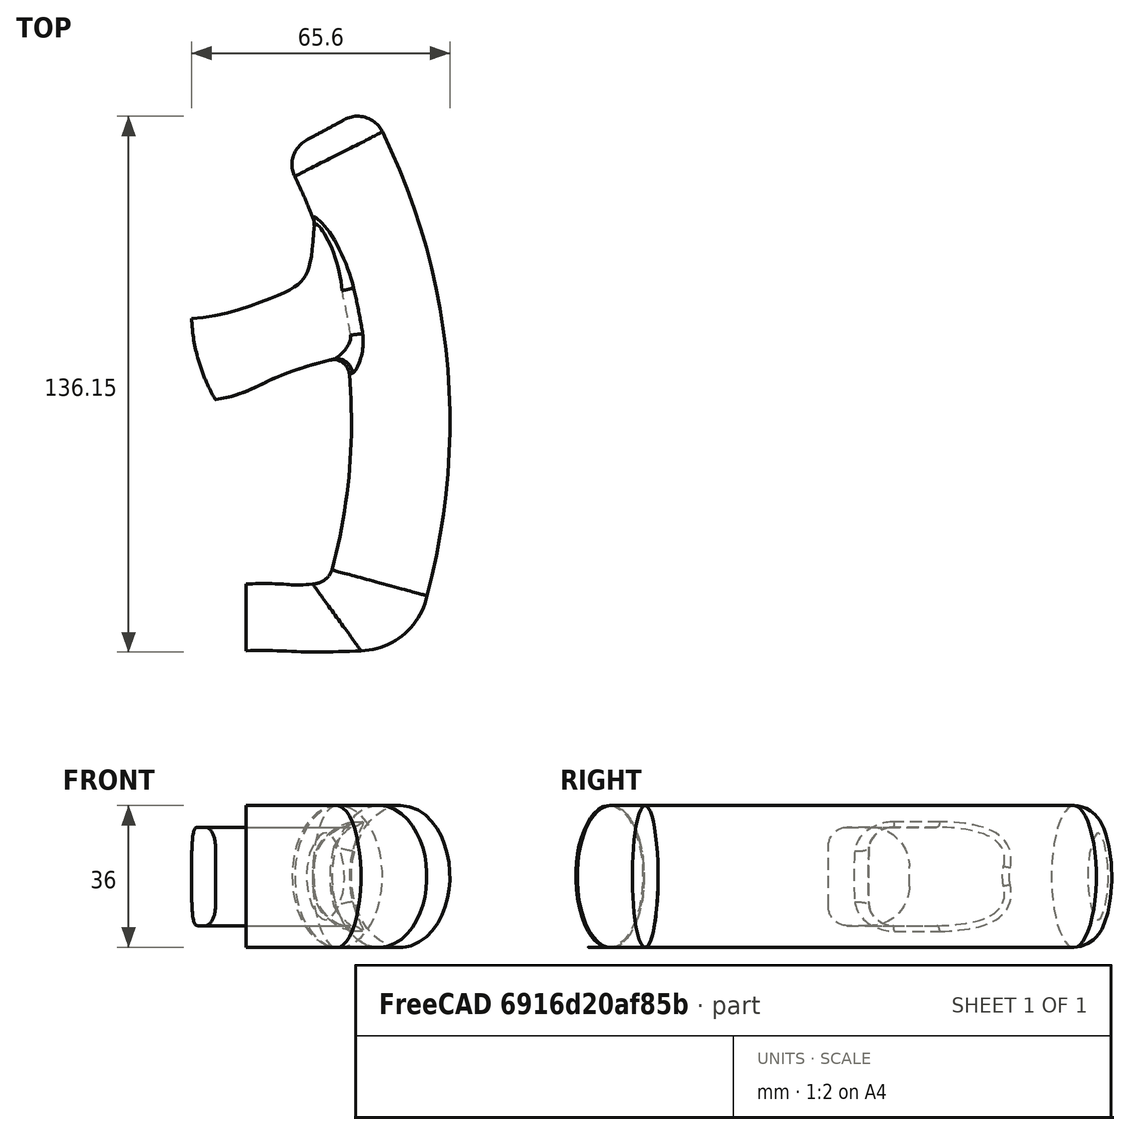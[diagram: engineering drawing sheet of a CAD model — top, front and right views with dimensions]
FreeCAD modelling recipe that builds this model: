
FCSTD DOCUMENT  (FreeCAD 1.0R39109 (Git))
Label: handle-5mk2
License: All rights reserved
LicenseURL: https://en.wikipedia.org/wiki/All_rights_reserved
objects: Sketcher::SketchObject×24, PartDesign::Plane×14, PartDesign::Fillet×6, PartDesign::AdditivePipe×3, Mesh::Feature×1, PartDesign::Pad×1, PartDesign::Body×1
note: 93 computed .brp shape members not serialized (recipe doc carries the construction recipe); baked Part::Feature solids carry a one-line shape summary decoded from their .brp

FEATURE [Sketcher::SketchObject] Sketch  label="draft"
  ArcFitTolerance = 1e-06
  FullyConstrained = false
  MakeInternals = false
  sketch-geometry (31):
    g0: LineSegment StartX=0 StartY=16.8405 StartZ=0 EndX=0 EndY=0 EndZ=0
    g1: ArcOfCircle CenterX=24.2442 CenterY=17 CenterZ=0 NormalX=0 NormalY=0 NormalZ=1 AngleXU=0 Radius=17 StartAngle=4.71239 EndAngle=6.01234
    g2: ArcOfCircle CenterX=12.089 CenterY=21.8405 CenterZ=0 NormalX=0 NormalY=0 NormalZ=1 AngleXU=0 Radius=5 StartAngle=4.71239 EndAngle=6.02249
    g3: ArcOfCircle CenterX=0 CenterY=8.42024 CenterZ=0 NormalX=0 NormalY=0 NormalZ=1 AngleXU=0 Radius=8.42024 StartAngle=1.5708 EndAngle=4.71239
    g4: LineSegment StartX=12.089 StartY=16.8405 StartZ=0 EndX=12.089 EndY=0 EndZ=0
    g5: LineSegment StartX=15.135 StartY=17.8754 StartZ=0 EndX=34.532 EndY=3.46632 EndZ=0
    g6: LineSegment StartX=12.089 StartY=16.8405 StartZ=0 EndX=24.2442 EndY=-0.00123973 EndZ=0
    g7: LineSegment StartX=16.92 StartY=20.5517 StartZ=0 EndX=40.6245 EndY=12.4517 EndZ=0
    g8: LineSegment StartX=12.089 StartY=16.8405 StartZ=0 EndX=17.9725 EndY=-3.6e-15 EndZ=0
    g9: LineSegment StartX=8.25203 StartY=67.8671 StartZ=0 EndX=4.47332 EndY=84.6059 EndZ=0
    g10: ArcOfCircle CenterX=6.36268 CenterY=76.2365 CenterZ=0 NormalX=0 NormalY=0 NormalZ=1 AngleXU=0 Radius=8.58001 StartAngle=1.79282 EndAngle=4.93441
    g11: LineSegment StartX=4.3823 StartY=126.388 StartZ=0 EndX=26.3634 EndY=138.297 EndZ=0
    g12: LineSegment StartX=0 StartY=0 StartZ=0 EndX=24.2442 EndY=0 EndZ=0
    g13: LineSegment StartX=12.089 StartY=16.8405 StartZ=0 EndX=0 EndY=16.8405 EndZ=0
    g14: ArcOfCircle CenterX=-122.373 CenterY=57.711 CenterZ=0 NormalX=0 NormalY=0 NormalZ=1 AngleXU=0 Radius=169.165 StartAngle=6.01234 EndAngle=6.77971
    g15: LineSegment StartX=34.0166 StartY=141.401 StartZ=0 EndX=34.0166 EndY=126.047 EndZ=0
    g16: LineSegment StartX=34.0166 StartY=141.401 StartZ=0 EndX=31.941 EndY=152.351 EndZ=0
    g17: LineSegment StartX=22.7796 StartY=155.606 StartZ=0 EndX=28.011 EndY=155.606 EndZ=0
    g18: LineSegment StartX=18.3769 StartY=88.901 StartZ=0 EndX=4.47332 EndY=84.6059 EndZ=0
    g19: LineSegment StartX=21.1969 StartY=70.7893 StartZ=0 EndX=8.25203 EndY=67.8671 EndZ=0
    g20: LineSegment StartX=18.7796 StartY=146.991 StartZ=0 EndX=18.7796 EndY=151.606 EndZ=0
    g21: LineSegment StartX=15.6305 StartY=135.869 StartZ=0 EndX=18.5135 EndY=145.224 EndZ=0
    g22: ArcOfCircle CenterX=12.7796 CenterY=146.991 CenterZ=0 NormalX=0 NormalY=0 NormalZ=1 AngleXU=0 Radius=6 StartAngle=5.98426 EndAngle=6.28319
    g23: ArcOfCircle CenterX=5.11835 CenterY=139.108 CenterZ=0 NormalX=0 NormalY=0 NormalZ=1 AngleXU=0 Radius=11 StartAngle=5.12409 EndAngle=5.98426
    g24: ArcOfCircle CenterX=27.9086 CenterY=86.9159 CenterZ=0 NormalX=0 NormalY=0 NormalZ=1 AngleXU=0 Radius=45.9511 StartAngle=1.9825 EndAngle=2.10829
    g25: ArcOfCircle CenterX=22.7796 CenterY=151.606 CenterZ=0 NormalX=0 NormalY=0 NormalZ=1 AngleXU=0 Radius=4 StartAngle=1.5708 EndAngle=3.14159
    g26: ArcOfCircle CenterX=28.011 CenterY=151.606 CenterZ=0 NormalX=0 NormalY=0 NormalZ=1 AngleXU=0 Radius=4 StartAngle=0.187333 EndAngle=1.5708
    g27: ArcOfCircle CenterX=54.0166 CenterY=126.047 CenterZ=0 NormalX=0 NormalY=0 NormalZ=1 AngleXU=0 Radius=20 StartAngle=3.14159 EndAngle=3.5112
    g28: ArcOfCircle CenterX=-122.373 CenterY=57.711 CenterZ=0 NormalX=0 NormalY=0 NormalZ=1 AngleXU=0 Radius=144.165 StartAngle=6.02249 EndAngle=6.37403
    g29: ArcOfCircle CenterX=-122.373 CenterY=57.711 CenterZ=0 NormalX=0 NormalY=0 NormalZ=1 AngleXU=0 Radius=144.165 StartAngle=0.218074 EndAngle=0.496528
    g30: ArcOfCircle CenterX=-122.373 CenterY=57.711 CenterZ=0 NormalX=0 NormalY=0 NormalZ=1 AngleXU=0 Radius=156.665 StartAngle=6.01234 EndAngle=6.77971
  constraints (1):
    c: Distance(g6,g6) = 20.77
FEATURE [Sketcher::SketchObject] Sketch001  label="main"
  ArcFitTolerance = 1e-06
  AttachmentSupport = -> [XY_Plane]
  FullyConstrained = false
  MakeInternals = false
  MapMode = 5
  sketch-geometry (33):
    g0: LineSegment StartX=0 StartY=0 StartZ=0 EndX=3e-16 EndY=17 EndZ=0
    g1: LineSegment StartX=3e-16 StartY=17 StartZ=0 EndX=11.9553 EndY=17 EndZ=0
    g2: ArcOfCircle CenterX=0.098169 CenterY=8.5 CenterZ=0 NormalX=0 NormalY=0 NormalZ=1 AngleXU=0 Radius=8.50057 StartAngle=1.58235 EndAngle=4.70084
    g3: LineSegment StartX=4.3731 StartY=126.451 StartZ=0 EndX=26.3546 EndY=138.359 EndZ=0
    g4: ArcOfCircle CenterX=-121.158 CenterY=57.9598 CenterZ=0 NormalX=0 NormalY=0 NormalZ=1 AngleXU=0 Radius=168 StartAngle=6.01838 EndAngle=6.78221
    g5: ArcOfCircle CenterX=-121.158 CenterY=57.9598 CenterZ=0 NormalX=0 NormalY=0 NormalZ=1 AngleXU=0 Radius=143 StartAngle=6.01836 EndAngle=6.78265
    g6: ArcOfCircle CenterX=11.9915 CenterY=22.1177 CenterZ=0 NormalX=0 NormalY=0 NormalZ=1 AngleXU=0 Radius=5.11783 StartAngle=4.70532 EndAngle=5.96793
    g7: LineSegment StartX=40.9861 StartY=13.99 StartZ=0 EndX=16.8571 EndY=20.5309 EndZ=0
    g8: ArcOfCircle CenterX=23.8596 CenterY=17.4727 CenterZ=0 NormalX=0 NormalY=0 NormalZ=1 AngleXU=0 Radius=17.4771 StartAngle=4.73473 EndAngle=6.08257
    g9: LineSegment StartX=33.9499 StartY=141.42 StartZ=0 EndX=32 EndY=152 EndZ=0
    g10: LineSegment StartX=19 StartY=152 StartZ=0 EndX=18.6911 EndY=146 EndZ=0
    g11: LineSegment StartX=22 StartY=155.6 StartZ=0 EndX=29 EndY=155.6 EndZ=0
    g12: ArcOfCircle CenterX=28.2135 CenterY=151.895 CenterZ=0 NormalX=0 NormalY=0 NormalZ=1 AngleXU=0 Radius=3.78792 StartAngle=0.027823 EndAngle=1.36165
    g13: ArcOfCircle CenterX=22.5443 CenterY=152.096 CenterZ=0 NormalX=0 NormalY=0 NormalZ=1 AngleXU=0 Radius=3.5456 StartAngle=1.72492 EndAngle=3.16879
    g14: LineSegment StartX=4.41682 StartY=84.6096 StartZ=0 EndX=8.23235 EndY=68.0434 EndZ=0
    g15: ArcOfCircle CenterX=6.32458 CenterY=76.3265 CenterZ=0 NormalX=0 NormalY=0 NormalZ=1 AngleXU=0 Radius=8.5 StartAngle=1.79717 EndAngle=4.93946
    g16: LineSegment StartX=4.42825 StartY=84.5878 StartZ=0 EndX=18.4319 EndY=88.947 EndZ=0
    g17: LineSegment StartX=8.23235 StartY=68.0434 StartZ=0 EndX=21.1452 EndY=72.063 EndZ=0
    g18: LineSegment StartX=32.5262 StartY=20 StartZ=0 EndX=28.9216 EndY=17.2604 EndZ=0
    g19: LineSegment StartX=11.9553 StartY=17 StartZ=0 EndX=24.25 EndY=5.33e-14 EndZ=0
    g20: LineSegment StartX=14.9929 StartY=17.9724 StartZ=0 EndX=35.0562 EndY=4.05322 EndZ=0
    g21: LineSegment StartX=16.2172 StartY=19.2306 StartZ=0 EndX=39.0494 EndY=8.82884 EndZ=0
    g22: LineSegment StartX=13.6942 StartY=17.2914 StartZ=0 EndX=30.2927 EndY=1.22269 EndZ=0
    g23: LineSegment StartX=10.6374 StartY=17 StartZ=0 EndX=17.3604 EndY=0 EndZ=0
    g24: LineSegment StartX=9.44468 StartY=17 StartZ=0 EndX=12.125 EndY=0 EndZ=0
    g25: LineSegment StartX=8.01497 StartY=17 StartZ=0 EndX=8.01497 EndY=0 EndZ=0
    g26: LineSegment StartX=5.97763 StartY=17 StartZ=0 EndX=5.97763 EndY=0 EndZ=0
    g27: LineSegment StartX=20.8595 StartY=74.6968 StartZ=0 EndX=45.6917 EndY=77.5875 EndZ=0
    g28: LineSegment StartX=0 StartY=0 StartZ=0 EndX=8.01497 EndY=0 EndZ=0
    g29: LineSegment StartX=8.01497 StartY=0 StartZ=0 EndX=24.25 EndY=0 EndZ=0
    g30: LineSegment StartX=15.3638 StartY=132.405 StartZ=0 EndX=18.6911 EndY=146 EndZ=0
    g31: LineSegment StartX=33.9499 StartY=141.42 StartZ=0 EndX=35.5663 EndY=109.757 EndZ=0
    g32: LineSegment StartX=15.3638 StartY=132.405 StartZ=0 EndX=35.5663 EndY=109.757 EndZ=0
  constraints (60):
    c: PointOnObject(g8,g-1)
    c: Distance(g0) = 17
    c: PointOnObject(g0,g-2)
    c: DistanceX(g-1,g8) = 24.25
    c: Coincident(g1,g0)
    c: Horizontal(g1)
    c: Coincident(g2,g0)
    c: Distance(g3) = 25
    c: Coincident(g4,g3)
    c: Radius(g4) = 168
    c: Coincident(g5,g4)
    c: Coincident(g5,g3)
    c: Coincident(g6,g1)
    c: Coincident(g6,g5)
    c: Coincident(g7,g4)
    c: Coincident(g7,g5)
    c: DistanceY(g-1,g4) = 13.99
    c: Coincident(g8,g4)
    c: Horizontal(g11)
    c: Coincident(g12,g11)
    c: Coincident(g12,g9)
    c: Coincident(g13,g11)
    c: Coincident(g13,g10)
    c: Distance(g14) = 17
    c: Symmetric(g14,g14,g15)
    c: Coincident(g15,g14)
    c: Coincident(g17,g14)
    c: PointOnObject(g17,g5)
    c: Parallel(g17,g16)
    c: Symmetric(g7,g7,g18)
    c: Coincident(g19,g1)
    c: PointOnObject(g20,g6)
    c: PointOnObject(g20,g8)
    c: PointOnObject(g21,g6)
    c: PointOnObject(g21,g8)
    c: PointOnObject(g22,g6)
    c: PointOnObject(g22,g8)
    c: PointOnObject(g23,g1)
    c: PointOnObject(g24,g1)
    c: Symmetric(g-1,g8,g24)
    c: PointOnObject(g25,g1)
    c: Vertical(g25)
    c: Symmetric(g1,g1,g26)
    c: Vertical(g26)
    c: PointOnObject(g27,g5)
    c: PointOnObject(g27,g4)
    c: Distance(g19,g19) = 20.98
    c: Distance(g21,g21) = 25.09
    c: Distance(g24,g24) = 17.21
    c: Coincident(g28,g0)
    c: Coincident(g28,g25)
    c: Horizontal(g28)
    c: Coincident(g29,g25)
    c: Coincident(g29,g8)
    c: Horizontal(g29)
    c: Symmetric(g3,g3,g30)
    c: Coincident(g30,g10)
    c: Coincident(g31,g9)
    c: Coincident(g32,g30)
    c: Coincident(g32,g31)
FEATURE [PartDesign::Plane] DatumPlane001
  AttachmentOffset = pos=(0,0,0) rot=(0,1,0;1.5708rad)
  AttachmentSupport = -> [Sketch001]
  Length = 197.115
  MapMode = 7
  Placement = pos=(40.9861,13.99,0) rot=(0.093727,0.703994,0.703994;2.95468rad)
  ResizeMode = 0
  Width = 68.8804
FEATURE [PartDesign::Plane] DatumPlane002
  AttachmentOffset = pos=(0,0,0) rot=(0,1,0;1.5708rad)
  AttachmentSupport = -> [Sketch001]
  Length = 181.364
  MapMode = 7
  Placement = pos=(0,0,0) rot=(0.57735,0.57735,0.57735;2.0944rad)
  ResizeMode = 0
  Width = 68.0717
FEATURE [PartDesign::Plane] DatumPlane
  AttachmentOffset = pos=(0,0,0) rot=(0,1,0;1.5708rad)
  AttachmentSupport = -> [Sketch001]
  Length = 221.295
  MapMode = 7
  Placement = pos=(4.3731,126.451,0) rot=(0.941347,0.238607,0.238607;1.6312rad)
  ResizeMode = 0
  Width = 70.0616
FEATURE [Sketcher::SketchObject] Sketch002
  ArcFitTolerance = 1e-06
  AttachmentSupport = -> [DatumPlane]
  FullyConstrained = false
  MakeInternals = false
  MapMode = 5
  Placement = pos=(4.3731,126.451,0) rot=(0.941347,0.238607,0.238607;1.6312rad)
  sketch-geometry (5):
    g0: Ellipse CenterX=12.5 CenterY=0 CenterZ=0 NormalX=0 NormalY=0 NormalZ=1 MajorRadius=18 MinorRadius=12.5 AngleXU=1.5708
    g1: LineSegment [constr] StartX=12.5 StartY=18 StartZ=0 EndX=12.5 EndY=-18 EndZ=0
    g2: LineSegment [constr] StartX=0 StartY=0 StartZ=0 EndX=25 EndY=0 EndZ=0
    g3: GeomPoint [constr] X=12.5 Y=12.9518 Z=0
    g4: GeomPoint [constr] X=12.5 Y=-12.9518 Z=0
  constraints (2):
    c: InternalAlignment(g1-g4 -> g0) x4
    c: PointOnObject(g-1,g0)
FEATURE [Sketcher::SketchObject] Sketch004
  ArcFitTolerance = 1e-06
  AttachmentOffset = pos=(0,0,-5) rot=(0,0,1;0rad)
  AttachmentSupport = -> [DatumPlane002]
  FullyConstrained = false
  MakeInternals = false
  MapMode = 5
  Placement = pos=(-5,0,0) rot=(0.57735,0.57735,0.57735;2.0944rad)
  sketch-geometry (5):
    g0: Ellipse CenterX=8.5 CenterY=0 CenterZ=0 NormalX=0 NormalY=0 NormalZ=1 MajorRadius=18 MinorRadius=8.5 AngleXU=1.5708
    g1: LineSegment [constr] StartX=8.5 StartY=18 StartZ=0 EndX=8.5 EndY=-18 EndZ=0
    g2: LineSegment [constr] StartX=0 StartY=0 StartZ=0 EndX=17 EndY=0 EndZ=0
    g3: GeomPoint [constr] X=8.5 Y=15.8666 Z=0
    g4: GeomPoint [constr] X=8.5 Y=-15.8666 Z=0
  constraints (2):
    c: InternalAlignment(g1-g4 -> g0) x4
    c: PointOnObject(g-1,g0)
FEATURE [PartDesign::AdditivePipe] AdditivePipe
  AuxilleryCurvelinear = true
  AuxillerySpineTangent = false
  Binormal = (0,0,0)
  Mode = 0
  Placement = pos=(4.3731,126.451,0) rot=(0.941347,0.238607,0.238607;1.6312rad)
  Profile = -> Sketch002
  Refine = true
  Spine = -> Sketch001 [Edge8]
  SpineTangent = false
  Suppressed = false
  Transformation = 0
  Transition = 0
FEATURE [PartDesign::Plane] DatumPlane004
  AttachmentOffset = pos=(0,0,0) rot=(0,1,0;1.5708rad)
  AttachmentSupport = -> [Sketch001]
  Length = 228.856
  MapMode = 7
  Placement = pos=(14.9929,17.9724,0) rot=(-0.91446,0.28615,0.28615;4.62309rad)
  ResizeMode = 0
  Width = 70.4176
FEATURE [Sketcher::SketchObject] Sketch006
  ArcFitTolerance = 1e-06
  AttachmentSupport = -> [DatumPlane004]
  FullyConstrained = false
  MakeInternals = false
  MapMode = 5
  Placement = pos=(14.9929,17.9724,0) rot=(0.91446,-0.28615,-0.28615;1.6601rad)
  sketch-geometry (5):
    g0: Ellipse CenterX=12.205 CenterY=0 CenterZ=0 NormalX=0 NormalY=0 NormalZ=1 MajorRadius=18 MinorRadius=12.205 AngleXU=1.5708
    g1: LineSegment [constr] StartX=12.205 StartY=18 StartZ=0 EndX=12.205 EndY=-18 EndZ=0
    g2: LineSegment [constr] StartX=0 StartY=0 StartZ=0 EndX=24.41 EndY=0 EndZ=0
    g3: GeomPoint [constr] X=12.205 Y=13.2302 Z=0
    g4: GeomPoint [constr] X=12.205 Y=-13.2302 Z=0
  constraints (2):
    c: InternalAlignment(g1-g4 -> g0) x4
    c: PointOnObject(g-1,g0)
FEATURE [PartDesign::Plane] DatumPlane005
  AttachmentOffset = pos=(0,0,0) rot=(0,1,0;1.5708rad)
  AttachmentSupport = -> [Sketch001]
  Length = 235.311
  MapMode = 7
  Placement = pos=(11.9553,17,0) rot=(-0.810565,0.414116,0.414116;4.50389rad)
  ResizeMode = 0
  Width = 70.7169
FEATURE [Sketcher::SketchObject] Sketch007
  ArcFitTolerance = 1e-06
  AttachmentSupport = -> [DatumPlane005]
  FullyConstrained = false
  MakeInternals = false
  MapMode = 5
  Placement = pos=(11.9553,17,0) rot=(0.810565,-0.414116,-0.414116;1.77929rad)
  sketch-geometry (5):
    g0: Ellipse CenterX=10.49 CenterY=0 CenterZ=0 NormalX=0 NormalY=0 NormalZ=1 MajorRadius=18 MinorRadius=10.49 AngleXU=1.5708
    g1: LineSegment [constr] StartX=10.49 StartY=18 StartZ=0 EndX=10.49 EndY=-18 EndZ=0
    g2: LineSegment [constr] StartX=0 StartY=0 StartZ=0 EndX=20.98 EndY=0 EndZ=0
    g3: GeomPoint [constr] X=10.49 Y=14.6274 Z=0
    g4: GeomPoint [constr] X=10.49 Y=-14.6274 Z=0
  constraints (2):
    c: InternalAlignment(g1-g4 -> g0) x4
    c: PointOnObject(g-1,g0)
FEATURE [PartDesign::Plane] DatumPlane006
  AttachmentOffset = pos=(0,0,0) rot=(0,1,0;1.5708rad)
  AttachmentSupport = -> [Sketch001]
  Length = 215.238
  MapMode = 7
  Placement = pos=(16.2172,19.2306,0) rot=(-0.955975,0.207499,0.207499;4.66738rad)
  ResizeMode = 0
  Width = 69.772
FEATURE [Sketcher::SketchObject] Sketch008
  ArcFitTolerance = 1e-06
  AttachmentSupport = -> [DatumPlane006]
  FullyConstrained = false
  MakeInternals = false
  MapMode = 5
  Placement = pos=(16.2172,19.2306,0) rot=(0.955975,-0.207499,-0.207499;1.6158rad)
  sketch-geometry (5):
    g0: Ellipse CenterX=12.545 CenterY=0 CenterZ=0 NormalX=0 NormalY=0 NormalZ=1 MajorRadius=18 MinorRadius=12.545 AngleXU=1.5708
    g1: LineSegment [constr] StartX=12.545 StartY=18 StartZ=0 EndX=12.545 EndY=-18 EndZ=0
    g2: LineSegment [constr] StartX=0 StartY=0 StartZ=0 EndX=25.09 EndY=0 EndZ=0
    g3: GeomPoint [constr] X=12.545 Y=12.9083 Z=0
    g4: GeomPoint [constr] X=12.545 Y=-12.9083 Z=0
  constraints (2):
    c: InternalAlignment(g1-g4 -> g0) x4
    c: PointOnObject(g-1,g0)
FEATURE [PartDesign::Plane] DatumPlane007
  AttachmentOffset = pos=(0,0,0) rot=(0,1,0;1.5708rad)
  AttachmentSupport = -> [Sketch001]
  Length = 235.311
  MapMode = 7
  Placement = pos=(11.9553,17,0) rot=(-0.810565,0.414116,0.414116;4.50389rad)
  ResizeMode = 0
  Width = 70.7169
FEATURE [Sketcher::SketchObject] Sketch009  label="Sketch009 7 dupe"
  ArcFitTolerance = 1e-06
  AttachmentSupport = -> [DatumPlane007]
  FullyConstrained = false
  MakeInternals = false
  MapMode = 5
  Placement = pos=(11.9553,17,0) rot=(0.810565,-0.414116,-0.414116;1.77929rad)
  sketch-geometry (5):
    g0: Ellipse CenterX=10.49 CenterY=0 CenterZ=0 NormalX=0 NormalY=0 NormalZ=1 MajorRadius=18 MinorRadius=10.49 AngleXU=1.5708
    g1: LineSegment [constr] StartX=10.49 StartY=18 StartZ=0 EndX=10.49 EndY=-18 EndZ=0
    g2: LineSegment [constr] StartX=0 StartY=0 StartZ=0 EndX=20.98 EndY=0 EndZ=0
    g3: GeomPoint [constr] X=10.49 Y=14.6274 Z=0
    g4: GeomPoint [constr] X=10.49 Y=-14.6274 Z=0
  constraints (2):
    c: InternalAlignment(g1-g4 -> g0) x4
    c: PointOnObject(g-1,g0)
FEATURE [PartDesign::Plane] DatumPlane008
  AttachmentOffset = pos=(0,0,0) rot=(0,1,0;1.5708rad)
  AttachmentSupport = -> [Sketch001]
  Length = 202.306
  MapMode = 7
  Placement = pos=(9.44468,17,0) rot=(-0.63745,0.54482,0.54482;4.2766rad)
  ResizeMode = 0
  Width = 69.1398
FEATURE [Sketcher::SketchObject] Sketch010
  ArcFitTolerance = 1e-06
  AttachmentOffset = pos=(0,0,2) rot=(0,0,1;0rad)
  AttachmentSupport = -> [DatumPlane008]
  FullyConstrained = false
  MakeInternals = false
  MapMode = 5
  Placement = pos=(7.46909,16.6885,2e-16) rot=(0.63745,-0.54482,-0.54482;2.00659rad)
  sketch-geometry (5):
    g0: Ellipse CenterX=8.605 CenterY=0 CenterZ=0 NormalX=0 NormalY=0 NormalZ=1 MajorRadius=18 MinorRadius=8.605 AngleXU=1.5708
    g1: LineSegment [constr] StartX=8.605 StartY=18 StartZ=0 EndX=8.605 EndY=-18 EndZ=0
    g2: LineSegment [constr] StartX=0 StartY=0 StartZ=0 EndX=17.21 EndY=0 EndZ=0
    g3: GeomPoint [constr] X=8.605 Y=15.8099 Z=0
    g4: GeomPoint [constr] X=8.605 Y=-15.8099 Z=0
  constraints (2):
    c: InternalAlignment(g1-g4 -> g0) x4
    c: PointOnObject(g-1,g0)
FEATURE [PartDesign::Plane] DatumPlane009
  AttachmentOffset = pos=(0,0,0) rot=(0,1,0;1.5708rad)
  AttachmentSupport = -> [Sketch001]
  Length = 181.364
  MapMode = 7
  Placement = pos=(8.01497,17,0) rot=(-0.57735,0.57735,0.57735;4.18879rad)
  ResizeMode = 0
  Width = 68.0717
FEATURE [Sketcher::SketchObject] Sketch011
  ArcFitTolerance = 1e-06
  AttachmentOffset = pos=(0,0,5) rot=(0,0,1;0rad)
  AttachmentSupport = -> [DatumPlane009]
  FullyConstrained = false
  MakeInternals = false
  MapMode = 5
  Placement = pos=(3.01497,17,0) rot=(0.57735,-0.57735,-0.57735;2.0944rad)
  sketch-geometry (5):
    g0: Ellipse CenterX=8.5 CenterY=0 CenterZ=0 NormalX=0 NormalY=0 NormalZ=1 MajorRadius=18 MinorRadius=8.5 AngleXU=1.5708
    g1: LineSegment [constr] StartX=8.5 StartY=18 StartZ=0 EndX=8.5 EndY=-18 EndZ=0
    g2: LineSegment [constr] StartX=0 StartY=0 StartZ=0 EndX=17 EndY=0 EndZ=0
    g3: GeomPoint [constr] X=8.5 Y=15.8666 Z=0
    g4: GeomPoint [constr] X=8.5 Y=-15.8666 Z=0
  constraints (2):
    c: InternalAlignment(g1-g4 -> g0) x4
    c: PointOnObject(g-1,g0)
FEATURE [Sketcher::SketchObject] Sketch012
  ArcFitTolerance = 1e-06
  AttachmentSupport = -> [XY_Plane]
  FullyConstrained = false
  MakeInternals = false
  MapMode = 5
  sketch-geometry (2):
    g0: ArcOfCircle CenterX=0 CenterY=8.5 CenterZ=0 NormalX=0 NormalY=0 NormalZ=1 AngleXU=0 Radius=8.5 StartAngle=1.5708 EndAngle=4.71239
    g1: LineSegment StartX=-1.6e-15 StartY=17 StartZ=0 EndX=-1.6e-15 EndY=0 EndZ=0
  constraints (4):
    c: Coincident(g0,g-1)
    c: Coincident(g1,g0)
    c: Coincident(g1,g0)
    c: Vertical(g1)
FEATURE [Sketcher::SketchObject] Sketch013
  ArcFitTolerance = 1e-06
  AttachmentOffset = pos=(0,0,12.5) rot=(0,0,1;0rad)
  AttachmentSupport = -> [XY_Plane]
  FullyConstrained = false
  MakeInternals = false
  MapMode = 5
  Placement = pos=(0,0,12.5) rot=(0,0,1;0rad)
  sketch-geometry (2):
    g0: Circle CenterX=29.902 CenterY=19.7627 CenterZ=0 NormalX=0 NormalY=0 NormalZ=1 AngleXU=0 Radius=0.75
    g1: Circle CenterX=24.3839 CenterY=114.1 CenterZ=0 NormalX=0 NormalY=0 NormalZ=1 AngleXU=0 Radius=0.75
  constraints (2):
    c: Diameter(g0) = 1.5
    c: Diameter(g1) = 1.5
FEATURE [Sketcher::SketchObject] Sketch014
  ArcFitTolerance = 1e-06
  AttachmentSupport = -> [XY_Plane]
  FullyConstrained = true
  MakeInternals = false
  MapMode = 5
FEATURE [Sketcher::SketchObject] Sketch015
  ArcFitTolerance = 1e-06
  AttachmentSupport = -> [XY_Plane]
  FullyConstrained = false
  MakeInternals = false
  MapMode = 5
  sketch-geometry (8):
    g0: LineSegment StartX=23.8504 StartY=155.6 StartZ=0 EndX=28.2953 EndY=155.6 EndZ=0
    g1: LineSegment StartX=18.9469 StartY=150.935 StartZ=0 EndX=18.7 EndY=145.978 EndZ=0
    g2: LineSegment StartX=18.7 StartY=145.978 StartZ=0 EndX=15.4 EndY=132.3 EndZ=0
    g3: LineSegment StartX=15.4 StartY=132.3 StartZ=0 EndX=34 EndY=110 EndZ=0
    g4: LineSegment StartX=34 StartY=141 StartZ=0 EndX=34 EndY=110 EndZ=0
    g5: LineSegment StartX=34 StartY=141 StartZ=0 EndX=31.8911 EndY=152.599 EndZ=0
    g6: ArcOfCircle CenterX=28.2953 CenterY=151.945 CenterZ=0 NormalX=0 NormalY=0 NormalZ=1 AngleXU=0 Radius=3.65468 StartAngle=0.179853 EndAngle=1.5708
    g7: ArcOfCircle CenterX=23.8504 CenterY=150.69 CenterZ=0 NormalX=0 NormalY=0 NormalZ=1 AngleXU=0 Radius=4.90952 StartAngle=1.5708 EndAngle=3.09181
  constraints (10):
    c: Horizontal(g0)
    c: Coincident(g2,g1)
    c: Coincident(g3,g2)
    c: Coincident(g4,g3)
    c: Vertical(g4)
    c: Coincident(g5,g4)
    c: Tangent(g0,g6) = 1.5708
    c: Tangent(g5,g6) = -1.5708
    c: Tangent(g0,g7) = 1.5708
    c: Tangent(g1,g7) = -1.5708
FEATURE [Sketcher::SketchObject] Sketch016
  ArcFitTolerance = 1e-06
  AttachmentSupport = -> [XY_Plane]
  FullyConstrained = false
  MakeInternals = false
  MapMode = 5
  sketch-geometry (25):
    g0-g6: Circle [constr] x7 (B-spline internal-alignment scaffolding for g7; pole/knot coordinates omitted)
    g7: BSplineCurve PolesCount=7 KnotsCount=5 Degree=3 IsPeriodic=0
    g8-g12: GeomPoint [constr] x5 (B-spline internal-alignment scaffolding for g7; pole/knot coordinates omitted)
    g13-g17: Circle [constr] x5 (B-spline internal-alignment scaffolding for g18; pole/knot coordinates omitted)
    g18: BSplineCurve PolesCount=5 KnotsCount=3 Degree=3 IsPeriodic=0
    g19: GeomPoint [constr] X=-12.7091 Y=63.7884 Z=0
    g20: GeomPoint [constr] X=2.04903 Y=69.1377 Z=0
    g21: GeomPoint [constr] X=32.8092 Y=77.3228 Z=0
    g22: LineSegment StartX=12.6036 StartY=113.182 StartZ=0 EndX=25 EndY=113.182 EndZ=0
    g23: LineSegment StartX=32.8092 StartY=77.3228 StartZ=0 EndX=25 EndY=113.182 EndZ=0
    g24: ArcOfCircle CenterX=24.8454 CenterY=86.0078 CenterZ=0 NormalX=0 NormalY=0 NormalZ=1 AngleXU=0 Radius=43.6353 StartAngle=3.1793 EndAngle=3.67586
  constraints (17):
    c: Weight(g0) = 1
    c: Equal(g0, g1-g6) x6
    c: InternalAlignment(g0-g6 -> g7) x7
    c: InternalAlignment(g8-g12 -> g7) x5
    c: Weight(g13) = 1
    c: Equal(g13, g14-g17) x4
    c: InternalAlignment(g13-g17 -> g18) x5
    c: InternalAlignment(g19,g18)
    c: InternalAlignment(g20,g18)
    c: InternalAlignment(g21,g18)
    c: PointOnObject(g15,g-2)
    c: Coincident(g22,g7)
    c: Horizontal(g22)
    c: Coincident(g23,g18)
    c: Coincident(g23,g22)
    c: Coincident(g24,g7)
    c: Coincident(g24,g18)
FEATURE [Mesh::Feature] right_handle
  Placement = pos=(-103,67,0) rot=(0,0,1;0rad)
FEATURE [Sketcher::SketchObject] Sketch017
  ArcFitTolerance = 1e-06
  AttachmentSupport = -> [AdditivePipe]
  FullyConstrained = true
  MakeInternals = false
  MapMode = 5
  Placement = pos=(4.3731,126.451,0) rot=(-0.941347,-0.238607,0.238607;1.6312rad)
FEATURE [Sketcher::SketchObject] Sketch018
  ArcFitTolerance = 1e-06
  AttachmentSupport = -> [DatumPlane001]
  FullyConstrained = false
  MakeInternals = false
  MapMode = 5
  Placement = pos=(40.9861,13.99,0) rot=(0.093727,0.703994,0.703994;2.95468rad)
  sketch-geometry (5):
    g0: Ellipse CenterX=12.5017 CenterY=0 CenterZ=0 NormalX=0 NormalY=0 NormalZ=1 MajorRadius=18 MinorRadius=12.5017 AngleXU=1.5708
    g1: LineSegment [constr] StartX=12.5017 StartY=18 StartZ=0 EndX=12.5017 EndY=-18 EndZ=0
    g2: LineSegment [constr] StartX=0 StartY=0 StartZ=0 EndX=25.0033 EndY=0 EndZ=0
    g3: GeomPoint [constr] X=12.5017 Y=12.9502 Z=0
    g4: GeomPoint [constr] X=12.5017 Y=-12.9502 Z=0
  constraints (3):
    c: InternalAlignment(g1-g4 -> g0) x4
    c: Distance(g0,g1) = 18
    c: PointOnObject(g0,g-1)
FEATURE [PartDesign::AdditivePipe] AdditivePipe001
  AuxilleryCurvelinear = true
  AuxillerySpineTangent = false
  BaseFeature = -> AdditivePipe
  Binormal = (0,0,0)
  Mode = 0
  Placement = pos=(4.3731,126.451,0) rot=(0.941347,0.238607,0.238607;1.6312rad)
  Profile = -> Sketch018
  Refine = true
  Sections = -> [Sketch008,Sketch006,Sketch007]
  Spine = -> Sketch001 [Edge7]
  SpineTangent = false
  Suppressed = false
  Transformation = 1
  Transition = 0
FEATURE [PartDesign::AdditivePipe] AdditivePipe002
  AuxilleryCurvelinear = true
  AuxillerySpineTangent = false
  BaseFeature = -> AdditivePipe001
  Binormal = (0,0,0)
  Mode = 0
  Placement = pos=(4.3731,126.451,0) rot=(0.941347,0.238607,0.238607;1.6312rad)
  Profile = -> Sketch009
  Refine = true
  Sections = -> [Sketch010,Sketch011,Sketch004]
  Spine = -> Sketch001 [Edge6]
  SpineTangent = false
  Suppressed = false
  Transformation = 1
  Transition = 0
FEATURE [Sketcher::SketchObject] Sketch019
  ArcFitTolerance = 1e-06
  FullyConstrained = false
  MakeInternals = false
  Placement = pos=(70.7,403.5,0) rot=(0,0,1;0rad)
  sketch-geometry (71):
    g0: ArcOfCircle CenterX=-152.069 CenterY=-222.772 CenterZ=0 NormalX=0 NormalY=0 NormalZ=1 AngleXU=0 Radius=77.3239 StartAngle=4.75433 EndAngle=5.19077
    g1: ArcOfCircle CenterX=-280.471 CenterY=-386.318 CenterZ=0 NormalX=0 NormalY=0 NormalZ=1 AngleXU=0 Radius=17 StartAngle=3.40529 EndAngle=4.71239
    g2: LineSegment StartX=-244.178 StartY=-403.318 StartZ=0 EndX=-280.471 EndY=-403.318 EndZ=0
    g3: ArcOfCircle CenterX=-244.178 CenterY=-373.318 CenterZ=0 NormalX=0 NormalY=0 NormalZ=1 AngleXU=0 Radius=30 StartAngle=4.71239 EndAngle=5.10704
    g4: ArcOfCircle CenterX=-288.174 CenterY=-267.685 CenterZ=0 NormalX=0 NormalY=0 NormalZ=1 AngleXU=0 Radius=144.429 StartAngle=5.10704 EndAngle=5.1698
    g5: ArcOfCircle CenterX=-215.558 CenterY=-415.211 CenterZ=0 NormalX=0 NormalY=0 NormalZ=1 AngleXU=0 Radius=20 StartAngle=1.66649 EndAngle=2.0282
    g6: ArcOfCircle CenterX=-163.5 CenterY=-957.553 CenterZ=0 NormalX=0 NormalY=0 NormalZ=1 AngleXU=0 Radius=564.835 StartAngle=1.47229 EndAngle=1.66649
    g7: Circle CenterX=-163.5 CenterY=-354.5 CenterZ=0 NormalX=0 NormalY=0 NormalZ=-1 AngleXU=0 Radius=14.3449
    g8: ArcOfCircle CenterX=-46.5291 CenterY=-386.318 CenterZ=0 NormalX=0 NormalY=0 NormalZ=1 AngleXU=0 Radius=17 StartAngle=4.71239 EndAngle=6.01949
    g9: LineSegment StartX=-82.8222 StartY=-403.318 StartZ=0 EndX=-46.5291 EndY=-403.318 EndZ=0
    g10: ArcOfCircle CenterX=-46.5291 CenterY=-386.318 CenterZ=0 NormalX=0 NormalY=0 NormalZ=1 AngleXU=0 Radius=17 StartAngle=4.71239 EndAngle=6.01949
    g11: ArcOfCircle CenterX=-38.8263 CenterY=-267.685 CenterZ=0 NormalX=0 NormalY=0 NormalZ=1 AngleXU=0 Radius=144.429 StartAngle=4.25498 EndAngle=4.31774
    g12: ArcOfCircle CenterX=-82.8222 CenterY=-373.318 CenterZ=0 NormalX=0 NormalY=0 NormalZ=1 AngleXU=0 Radius=30 StartAngle=4.31774 EndAngle=4.71239
    g13: ArcOfCircle CenterX=-111.442 CenterY=-415.211 CenterZ=0 NormalX=0 NormalY=0 NormalZ=1 AngleXU=0 Radius=20 StartAngle=1.11339 EndAngle=1.4751
    g14: ArcOfCircle CenterX=-248.227 CenterY=-371.478 CenterZ=0 NormalX=0 NormalY=0 NormalZ=1 AngleXU=0 Radius=15 StartAngle=4.71239 EndAngle=6.22689
    g15: ArcOfCircle CenterX=-174.931 CenterY=-222.772 CenterZ=0 NormalX=0 NormalY=0 NormalZ=1 AngleXU=0 Radius=77.3239 StartAngle=4.23401 EndAngle=4.67045
    g16: ArcOfCircle CenterX=-78.7734 CenterY=-371.478 CenterZ=0 NormalX=0 NormalY=0 NormalZ=1 AngleXU=0 Radius=15 StartAngle=3.19789 EndAngle=4.71239
    g17: LineSegment StartX=-148.827 StartY=-300.028 StartZ=0 EndX=-178.173 EndY=-300.028 EndZ=0
    g18: LineSegment StartX=-58.6961 StartY=-386.478 StartZ=0 EndX=-78.7734 EndY=-386.478 EndZ=0
    g19: ArcOfCircle CenterX=-58.6961 CenterY=-381.478 CenterZ=0 NormalX=0 NormalY=0 NormalZ=1 AngleXU=0 Radius=5 StartAngle=4.71239 EndAngle=6.02246
    g20: Circle CenterX=-163.5 CenterY=-382.5 CenterZ=0 NormalX=0 NormalY=0 NormalZ=-1 AngleXU=0 Radius=2.5
    g21: Circle CenterX=-139.251 CenterY=-368.5 CenterZ=0 NormalX=0 NormalY=0 NormalZ=-1 AngleXU=0 Radius=2.5
    g22: Circle CenterX=-139.251 CenterY=-340.5 CenterZ=0 NormalX=0 NormalY=0 NormalZ=-1 AngleXU=0 Radius=2.5
    g23: Circle CenterX=-163.5 CenterY=-326.5 CenterZ=0 NormalX=0 NormalY=0 NormalZ=-1 AngleXU=0 Radius=2.5
    g24: Circle CenterX=-187.749 CenterY=-340.5 CenterZ=0 NormalX=0 NormalY=0 NormalZ=-1 AngleXU=0 Radius=2.5
    g25: Circle CenterX=-187.749 CenterY=-368.5 CenterZ=0 NormalX=0 NormalY=0 NormalZ=-1 AngleXU=0 Radius=2.5
    g26: LineSegment StartX=-56.0985 StartY=-267.155 StartZ=0 EndX=-53.2155 EndY=-257.799 EndZ=0
    g27: ArcOfCircle CenterX=-65.6551 CenterY=-264.21 CenterZ=0 NormalX=0 NormalY=0 NormalZ=1 AngleXU=0 Radius=10 StartAngle=5.12409 EndAngle=5.98426
    g28: ArcOfCircle CenterX=-57.9938 CenterY=-256.327 CenterZ=0 NormalX=0 NormalY=0 NormalZ=1 AngleXU=0 Radius=5 StartAngle=5.98426 EndAngle=8.10068
    g29: ArcOfCircle CenterX=-42.8649 CenterY=-316.402 CenterZ=0 NormalX=0 NormalY=0 NormalZ=1 AngleXU=0 Radius=66.9511 StartAngle=1.8175 EndAngle=3.69281
    g30: ArcOfCircle CenterX=-42.8649 CenterY=-316.402 CenterZ=0 NormalX=0 NormalY=0 NormalZ=1 AngleXU=0 Radius=68.9511 StartAngle=1.8031 EndAngle=2.51892
    g31: ArcOfCircle CenterX=-193.147 CenterY=-345.607 CenterZ=0 NormalX=0 NormalY=0 NormalZ=1 AngleXU=0 Radius=169.165 StartAngle=6.01194 EndAngle=6.87087
    g32: ArcOfCircle CenterX=-193.147 CenterY=-345.607 CenterZ=0 NormalX=0 NormalY=0 NormalZ=1 AngleXU=0 Radius=144.165 StartAngle=6.02246 EndAngle=6.87647
    g33: ArcOfCircle CenterX=-42.8649 CenterY=-316.402 CenterZ=0 NormalX=0 NormalY=0 NormalZ=1 AngleXU=0 Radius=46.9511 StartAngle=1.9825 EndAngle=3.61535
    g34: ArcOfCircle CenterX=-95.6403 CenterY=-348.847 CenterZ=0 NormalX=0 NormalY=0 NormalZ=1 AngleXU=0 Radius=5 StartAngle=3.69281 EndAngle=5.64052
    g35: LineSegment StartX=-85.0916 StartY=-343.1 StartZ=0 EndX=-91.6378 EndY=-351.844 EndZ=0
    g36: ArcOfCircle CenterX=-89.0941 CenterY=-340.104 CenterZ=0 NormalX=0 NormalY=0 NormalZ=1 AngleXU=0 Radius=5 StartAngle=5.64052 EndAngle=6.75694
    g37: ArcOfCircle CenterX=-60.2975 CenterY=-368.87 CenterZ=0 NormalX=0 NormalY=0 NormalZ=1 AngleXU=0 Radius=33.6298 StartAngle=2.9338 EndAngle=3.24442
    g38: LineSegment StartX=-48.5854 StartY=-313.24 StartZ=0 EndX=-88.8881 EndY=-325.69 EndZ=0
    g39: LineSegment StartX=-48.175 StartY=-332.212 StartZ=0 EndX=-74.392 EndY=-338.131 EndZ=0
    g40: LineSegment StartX=-83.0964 StartY=-343.773 StartZ=0 EndX=-87.8643 EndY=-350.141 EndZ=0
    g41: LineSegment StartX=-57.0129 StartY=-247.712 StartZ=0 EndX=-33.4816 EndY=-247.712 EndZ=0
    g42: LineSegment StartX=-36.7568 StartY=-261.917 StartZ=0 EndX=-40.5225 EndY=-242.051 EndZ=0
    g43: LineSegment StartX=-36.7568 StartY=-261.917 StartZ=0 EndX=-36.7568 EndY=-284.959 EndZ=0
    g44: ArcOfCircle CenterX=-284.135 CenterY=-316.402 CenterZ=0 NormalX=0 NormalY=0 NormalZ=1 AngleXU=0 Radius=66.9511 StartAngle=5.73197 EndAngle=7.60728
    g45: ArcOfCircle CenterX=-284.135 CenterY=-316.402 CenterZ=0 NormalX=0 NormalY=0 NormalZ=1 AngleXU=0 Radius=46.9511 StartAngle=5.80943 EndAngle=7.44228
    g46: LineSegment StartX=-241.908 StartY=-343.1 StartZ=0 EndX=-235.362 EndY=-351.844 EndZ=0
    g47: ArcOfCircle CenterX=-237.906 CenterY=-340.104 CenterZ=0 NormalX=0 NormalY=0 NormalZ=1 AngleXU=0 Radius=5 StartAngle=2.66784 EndAngle=3.78426
    g48: ArcOfCircle CenterX=-231.36 CenterY=-348.847 CenterZ=0 NormalX=0 NormalY=0 NormalZ=1 AngleXU=0 Radius=5 StartAngle=3.78426 EndAngle=5.73197
    g49: Circle CenterX=-231.444 CenterY=-338.014 CenterZ=0 NormalX=0 NormalY=0 NormalZ=-1 AngleXU=0 Radius=5
    g50: Circle CenterX=-227.384 CenterY=-321.17 CenterZ=0 NormalX=0 NormalY=0 NormalZ=-1 AngleXU=0 Radius=5
    g51: Circle CenterX=-228.577 CenterY=-303.884 CenterZ=0 NormalX=0 NormalY=0 NormalZ=-1 AngleXU=0 Radius=5
    g52: Circle CenterX=-234.913 CenterY=-287.756 CenterZ=0 NormalX=0 NormalY=0 NormalZ=-1 AngleXU=0 Radius=5
    g53: Circle CenterX=-245.805 CenterY=-274.281 CenterZ=0 NormalX=0 NormalY=0 NormalZ=-1 AngleXU=0 Radius=5
    g54: Circle CenterX=-260.245 CenterY=-264.704 CenterZ=0 NormalX=0 NormalY=0 NormalZ=-1 AngleXU=0 Radius=5
    g55: LineSegment StartX=-270.901 StartY=-267.155 StartZ=0 EndX=-273.784 EndY=-257.799 EndZ=0
    g56: ArcOfCircle CenterX=-269.006 CenterY=-256.327 CenterZ=0 NormalX=0 NormalY=0 NormalZ=1 AngleXU=0 Radius=5 StartAngle=1.32409 EndAngle=3.44052
    g57: ArcOfCircle CenterX=-261.345 CenterY=-264.21 CenterZ=0 NormalX=0 NormalY=0 NormalZ=1 AngleXU=0 Radius=10 StartAngle=3.44052 EndAngle=4.30068
    g58: ArcOfCircle CenterX=-284.135 CenterY=-316.402 CenterZ=0 NormalX=0 NormalY=0 NormalZ=1 AngleXU=0 Radius=68.9511 StartAngle=0.622676 EndAngle=1.3385
    g59: ArcOfCircle CenterX=-284.135 CenterY=-316.402 CenterZ=0 NormalX=0 NormalY=0 NormalZ=1 AngleXU=0 Radius=66.9511 StartAngle=5.73197 EndAngle=7.60728
    g60: LineSegment StartX=-269.987 StartY=-247.712 StartZ=0 EndX=-293.518 EndY=-247.712 EndZ=0
    g61: ArcOfCircle CenterX=-133.853 CenterY=-345.607 CenterZ=0 NormalX=0 NormalY=0 NormalZ=1 AngleXU=0 Radius=169.165 StartAngle=2.5539 EndAngle=3.41284
    g62: ArcOfCircle CenterX=-133.853 CenterY=-345.607 CenterZ=0 NormalX=0 NormalY=0 NormalZ=1 AngleXU=0 Radius=144.165 StartAngle=2.5483 EndAngle=3.40231
    g63: LineSegment StartX=-278.415 StartY=-313.24 StartZ=0 EndX=-238.112 EndY=-325.69 EndZ=0
    g64: LineSegment StartX=-278.825 StartY=-332.212 StartZ=0 EndX=-252.608 EndY=-338.131 EndZ=0
    g65: LineSegment StartX=-243.904 StartY=-343.773 StartZ=0 EndX=-239.136 EndY=-350.141 EndZ=0
    g66: ArcOfCircle CenterX=-266.703 CenterY=-368.87 CenterZ=0 NormalX=0 NormalY=0 NormalZ=1 AngleXU=0 Radius=33.6298 StartAngle=6.18035 EndAngle=6.49098
    g67: LineSegment StartX=-268.304 StartY=-386.478 StartZ=0 EndX=-248.227 EndY=-386.478 EndZ=0
    g68: ArcOfCircle CenterX=-268.304 CenterY=-381.478 CenterZ=0 NormalX=0 NormalY=0 NormalZ=1 AngleXU=0 Radius=5 StartAngle=3.40231 EndAngle=4.71239
    g69: LineSegment StartX=-290.243 StartY=-261.917 StartZ=0 EndX=-286.478 EndY=-242.051 EndZ=0
    g70: LineSegment StartX=-290.243 StartY=-261.917 StartZ=0 EndX=-290.243 EndY=-284.959 EndZ=0
FEATURE [PartDesign::Pad] Pad
  BaseFeature = -> AdditivePipe002
  Direction = (0,0,1)
  Length = 25
  Length2 = 10
  Midplane = true
  Placement = pos=(4.3731,126.451,0) rot=(0.941347,0.238607,0.238607;1.6312rad)
  Profile = -> Sketch016
  ReferenceAxis = -> Sketch016 [N_Axis]
  Refine = true
  Suppressed = false
  Type = 0
FEATURE [PartDesign::Fillet] Fillet
  Base = -> Pad [Edge27]
  BaseFeature = -> Pad
  Placement = pos=(4.3731,126.451,0) rot=(0.941347,0.238607,0.238607;1.6312rad)
  Radius = 5
  Refine = true
  SupportTransform = false
  Suppressed = false
  UseAllEdges = false
FEATURE [PartDesign::Fillet] Fillet001
  Base = -> Fillet [Edge26]
  BaseFeature = -> Fillet
  Placement = pos=(4.3731,126.451,0) rot=(0.941347,0.238607,0.238607;1.6312rad)
  Radius = 10
  Refine = true
  SupportTransform = false
  Suppressed = false
  UseAllEdges = false
FEATURE [PartDesign::Fillet] Fillet002
  Base = -> Fillet001 [Edge25]
  BaseFeature = -> Fillet001
  Placement = pos=(4.3731,126.451,0) rot=(0.941347,0.238607,0.238607;1.6312rad)
  Radius = 10
  Refine = true
  SupportTransform = false
  Suppressed = false
  UseAllEdges = false
FEATURE [PartDesign::Fillet] Fillet003
  Base = -> Fillet002 [Edge23]
  BaseFeature = -> Fillet002
  Placement = pos=(4.3731,126.451,0) rot=(0.941347,0.238607,0.238607;1.6312rad)
  Radius = 5
  Refine = true
  SupportTransform = false
  Suppressed = false
  UseAllEdges = false
FEATURE [PartDesign::Fillet] Fillet004
  Base = -> Fillet003 [Edge4]
  BaseFeature = -> Fillet003
  Placement = pos=(4.3731,126.451,0) rot=(0.941347,0.238607,0.238607;1.6312rad)
  Radius = 4
  Refine = true
  SupportTransform = false
  Suppressed = false
  UseAllEdges = false
FEATURE [Sketcher::SketchObject] Sketch020
  ArcFitTolerance = 1e-06
  AttachmentSupport = -> [XY_Plane]
  ExternalGeometry = -> [Sketch004]
  FullyConstrained = false
  MakeInternals = false
  MapMode = 5
  sketch-geometry (8):
    g0: LineSegment StartX=-5 StartY=17 StartZ=0 EndX=-8 EndY=17 EndZ=0
    g1: LineSegment StartX=-5 StartY=0 StartZ=0 EndX=-14 EndY=0 EndZ=0
    g2: ArcOfCircle CenterX=-8.30801 CenterY=31.9434 CenterZ=0 NormalX=0 NormalY=0 NormalZ=1 AngleXU=0 Radius=14.9466 StartAngle=3.50569 EndAngle=4.733
    g3: ArcOfCircle CenterX=-12.819 CenterY=29.0329 CenterZ=0 NormalX=0 NormalY=0 NormalZ=1 AngleXU=0 Radius=29.0569 StartAngle=4.09262 EndAngle=4.67173
    g4: LineSegment StartX=-29.6965 StartY=5.38017 StartZ=0 EndX=-22.2748 EndY=26.6209 EndZ=0
    g5: LineSegment StartX=-15.5855 StartY=18.8882 StartZ=0 EndX=-22.7937 EndY=1.74171 EndZ=0
    g6: LineSegment StartX=-14 StartY=0 StartZ=0 EndX=-10.9422 EndY=17.2308 EndZ=0
    g7: LineSegment StartX=-5 StartY=17 StartZ=0 EndX=-5 EndY=0 EndZ=0
  constraints (19):
    c: Distance(g0) = 3
    c: Coincident(g0,g-3)
    c: Horizontal(g0)
    c: Distance(g1) = 9
    c: Coincident(g1,g-3)
    c: PointOnObject(g1,g-1)
    c: Coincident(g2,g0)
    c: Coincident(g3,g1)
    c: Coincident(g4,g3)
    c: Coincident(g4,g2)
    c: PointOnObject(g5,g2)
    c: PointOnObject(g5,g3)
    c: Coincident(g6,g1)
    c: PointOnObject(g6,g2)
    c: Coincident(g7,g0)
    c: Coincident(g7,g1)
    c: Distance(g6,g6) = 17.5
    c: Distance(g5,g5) = 18.6
    c: Distance(g4,g4) = 22.5
FEATURE [PartDesign::Plane] DatumPlane010
  AttachmentOffset = pos=(0,0,0) rot=(0,1,0;1.5708rad)
  AttachmentSupport = -> [Sketch020]
  Length = 181.364
  MapMode = 7
  Placement = pos=(-5,17,0) rot=(-0.57735,0.57735,0.57735;4.18879rad)
  ResizeMode = 0
  Width = 68.0717
FEATURE [Sketcher::SketchObject] Sketch022
  ArcFitTolerance = 1e-06
  AttachmentSupport = -> [DatumPlane010]
  FullyConstrained = true
  MakeInternals = false
  MapMode = 5
  Placement = pos=(-5,17,0) rot=(0.57735,-0.57735,-0.57735;2.0944rad)
  sketch-geometry (5):
    g0: Ellipse CenterX=8.5 CenterY=0 CenterZ=0 NormalX=0 NormalY=0 NormalZ=1 MajorRadius=18 MinorRadius=8.5 AngleXU=1.5708
    g1: LineSegment [constr] StartX=8.5 StartY=18 StartZ=0 EndX=8.5 EndY=-18 EndZ=0
    g2: LineSegment [constr] StartX=2.89052e-11 StartY=0 StartZ=0 EndX=17 EndY=0 EndZ=0
    g3: GeomPoint [constr] X=8.5 Y=15.8666 Z=0
    g4: GeomPoint [constr] X=8.5 Y=-15.8666 Z=0
  constraints (6):
    c: InternalAlignment(g1-g4 -> g0) x4
    c: PointOnObject(g-1,g0)
    c: DistanceY(g1,g1) = 36
    c: DistanceX(g2,g2) = 17
    c: DistanceY(g2,g-1) = 0
    c: DistanceY(g-1,g2) = 0
FEATURE [PartDesign::Plane] DatumPlane011
  AttachmentOffset = pos=(0,0,0) rot=(0,1,0;1.5708rad)
  AttachmentSupport = -> [Sketch020]
  Length = 204.565
  MapMode = 7
  Placement = pos=(-14,-4e-16,0) rot=(0.644821,0.540465,0.540465;1.99614rad)
  ResizeMode = 0
  Width = 69.2517
FEATURE [Sketcher::SketchObject] Sketch023
  ArcFitTolerance = 1e-06
  AttachmentSupport = -> [DatumPlane011]
  FullyConstrained = false
  MakeInternals = false
  MapMode = 5
  Placement = pos=(-14,-4e-16,0) rot=(0.644821,0.540465,0.540465;1.99614rad)
  sketch-geometry (5):
    g0: Ellipse CenterX=8.75 CenterY=4e-16 CenterZ=0 NormalX=0 NormalY=0 NormalZ=1 MajorRadius=10 MinorRadius=8.75 AngleXU=1.56958
    g1: LineSegment [constr] StartX=8.76214 StartY=10 StartZ=0 EndX=8.73786 EndY=-10 EndZ=0
    g2: LineSegment [constr] StartX=7.95936e-06 StartY=0.0106227 StartZ=0 EndX=17.5 EndY=-0.0106227 EndZ=0
    g3: GeomPoint [constr] X=8.75588 Y=4.84124 Z=0
    g4: GeomPoint [constr] X=8.74413 Y=-4.84124 Z=0
  constraints (5):
    c: InternalAlignment(g1-g4 -> g0) x4
    c: PointOnObject(g-1,g0)
    c: DistanceY(g-1,g1) = 10
    c: DistanceX(g-1,g2) = 17.5
    c: DistanceY(g1,g-1) = 10
FEATURE [PartDesign::Plane] DatumPlane012
  AttachmentOffset = pos=(0,0,0) rot=(0,1,0;1.5708rad)
  AttachmentSupport = -> [Sketch020]
  Length = 225.189
  MapMode = 7
  Placement = pos=(-15.5855,18.8882,0) rot=(-0.425205,0.64,0.64;3.94568rad)
  ResizeMode = 0
  Width = 70.2456
FEATURE [Sketcher::SketchObject] Sketch024
  ArcFitTolerance = 1e-06
  AttachmentSupport = -> [DatumPlane012]
  FullyConstrained = false
  MakeInternals = false
  MapMode = 5
  Placement = pos=(-15.5855,18.8882,0) rot=(-0.425205,0.64,0.64;3.94568rad)
  sketch-geometry (5):
    g0: Ellipse CenterX=9.3 CenterY=0 CenterZ=0 NormalX=0 NormalY=0 NormalZ=1 MajorRadius=9.3 MinorRadius=5 AngleXU=0
    g1: LineSegment [constr] StartX=18.6 StartY=0 StartZ=0 EndX=0 EndY=0 EndZ=0
    g2: LineSegment [constr] StartX=9.3 StartY=5 StartZ=0 EndX=9.3 EndY=-5 EndZ=0
    g3: GeomPoint [constr] X=17.1416 Y=0 Z=0
    g4: GeomPoint [constr] X=1.45844 Y=0 Z=0
  constraints (4):
    c: InternalAlignment(g1-g4 -> g0) x4
    c: PointOnObject(g-1,g0)
    c: DistanceY(g2,g2) = 10
    c: DistanceX(g-1,g1) = 18.6
FEATURE [PartDesign::Plane] DatumPlane013
  AttachmentOffset = pos=(0,0,0) rot=(0,1,0;1.5708rad)
  AttachmentSupport = -> [Sketch020]
  Length = 220.489
  MapMode = 7
  Placement = pos=(-29.6965,5.38017,0) rot=(0.705724,0.500976,0.500976;1.91248rad)
  ResizeMode = 0
  Width = 70.0233
FEATURE [Sketcher::SketchObject] Sketch025
  ArcFitTolerance = 1e-06
  AttachmentSupport = -> [DatumPlane013]
  FullyConstrained = true
  MakeInternals = false
  MapMode = 5
  Placement = pos=(-29.6965,5.38017,0) rot=(0.705724,0.500976,0.500976;1.91248rad)
  sketch-geometry (7):
    g0: LineSegment StartX=0 StartY=0 StartZ=0 EndX=22.5 EndY=0 EndZ=0
    g1: Ellipse CenterX=11.25 CenterY=7.11103e-07 CenterZ=0 NormalX=0 NormalY=0 NormalZ=1 MajorRadius=11.25 MinorRadius=3 AngleXU=-1e-16
    g2: LineSegment [constr] StartX=22.5 StartY=7.11103e-07 StartZ=0 EndX=0 EndY=7.11103e-07 EndZ=0
    g3: LineSegment [constr] StartX=11.25 StartY=3 StartZ=0 EndX=11.25 EndY=-3 EndZ=0
    g4: GeomPoint [constr] X=22.0926 Y=7.11103e-07 Z=0
    g5: GeomPoint [constr] X=0.407376 Y=7.11103e-07 Z=0
    g6: GeomPoint X=11.25 Y=7.11103e-07 Z=0
  constraints (10):
    c: Distance(g0) = 22.5
    c: Coincident(g0,g-1)
    c: Horizontal(g0)
    c: InternalAlignment(g2-g5 -> g1) x4
    c: PointOnObject(g0,g1)
    c: PointOnObject(g0,g1)
    c: Angle(g-1,g3) = 1.5708
    c: DistanceY(g3,g3) = 6
    c: DistanceX(g2,g2) = 22.5
    c: Coincident(g6,g1)
FEATURE [PartDesign::Plane] DatumPlane014
  AttachmentOffset = pos=(0,0,0) rot=(-0.57735,0.57735,0.57735;2.0944rad)
  AttachmentSupport = -> [Fillet004]
  Length = 230.972
  MapMode = 2
  Placement = pos=(15.3638,132.405,2.8e-15) rot=(-0.388116,-0.651677,0.651677;2.40115rad)
  ResizeMode = 0
  Width = 70.5162
FEATURE [Sketcher::SketchObject] Sketch026
  ArcFitTolerance = 1e-06
  AttachmentSupport = -> [DatumPlane014]
  FullyConstrained = false
  MakeInternals = false
  MapMode = 5
  Placement = pos=(15.3638,132.405,2.8e-15) rot=(0.388116,0.651677,-0.651677;3.88203rad)
  sketch-geometry (3):
    g0: LineSegment StartX=0 StartY=18.5458 StartZ=0 EndX=-15.6339 EndY=18.5458 EndZ=0
    g1: LineSegment StartX=-15.6339 StartY=18.5458 StartZ=0 EndX=0 EndY=8.71786 EndZ=0
    g2: LineSegment StartX=0 StartY=8.71786 StartZ=0 EndX=0 EndY=18.5458 EndZ=0
  constraints (6):
    c: PointOnObject(g0,g-2)
    c: Horizontal(g0)
    c: Coincident(g0,g1)
    c: PointOnObject(g1,g-2)
    c: Coincident(g1,g2)
    c: Coincident(g2,g0)
FEATURE [PartDesign::Fillet] Fillet005
  Base = -> Fillet004 [Edge11]
  BaseFeature = -> Fillet004
  Placement = pos=(4.3731,126.451,0) rot=(0.941347,0.238607,0.238607;1.6312rad)
  Radius = 7
  Refine = true
  SupportTransform = false
  Suppressed = false
  UseAllEdges = false
FEATURE [PartDesign::Body] Body
  AllowCompound = false
  Group = -> [Sketch,Sketch001,DatumPlane,DatumPlane001,DatumPlane002,Sketch002,Sketch004,AdditivePipe,DatumPlane004,Sketch006,DatumPlane005,Sketch007,DatumPlane006,Sketch008,DatumPlane007,Sketch009,DatumPlane008,Sketch010,DatumPlane009,Sketch011,Sketch012,Sketch013,Sketch014,Sketch015,Sketch016,Sketch017,Sketch018,AdditivePipe001,AdditivePipe002,Pad,Fillet,Fillet001,Fillet002,Fillet003,Fillet004,Sketch020,+11 more]
  Origin = -> Origin
  Tip = -> Fillet005
